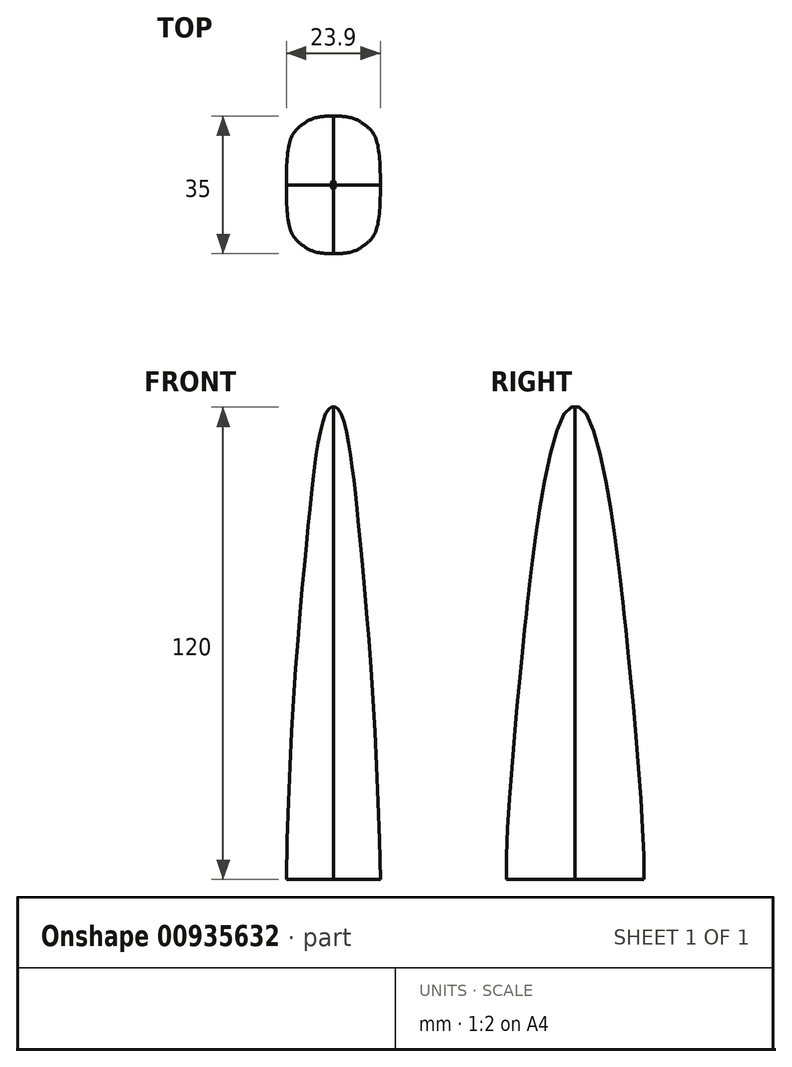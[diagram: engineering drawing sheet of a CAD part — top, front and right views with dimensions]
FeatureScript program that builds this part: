
annotation { "Feature Type Name" : "Feature", "Feature Type Description" : "" }
export const myFeature = defineFeature(function(context is Context, id is Id, definition is map)
    precondition{}
    {
        {
            var Q0;
            Q0=qCreatedBy(makeId("Top.planeOp"),FACE);
            var sketch = newSketch(context, id + "F0", { "sketchPlane" : qUnion([Q0])});
            skLineSegment(sketch, "E0", {"start": v(11.95, 0) * mm, "end": v(11.95, 33.1) * mm, "construction": true});
            skLineSegment(sketch, "E1", {"start": v(11.95, 0) * mm, "end": v(11.95, -38.84) * mm, "construction": true});
            skLineSegment(sketch, "E2", {"start": v(0, 0) * mm, "end": v(11.95, 0) * mm});
            skLineSegment(sketch, "E3", {"start": v(0, 0) * mm, "end": v(0, 17.5) * mm});
            skFitSpline(sketch, "E4", {"points": [v(0, 17.5) * mm, v(6.97, 15.94) * mm, v(9.26, 14.16) * mm, v(11.08, 10.92) * mm, v(11.95, 0) * mm], "startDerivative": vector(48.18, -0.54) * mm, "endDerivative": vector(0, -35.8) * mm});
            skSolve(sketch);
        }
        {
            var Q0;
            Q0=qCreatedBy(makeId("Top.planeOp"),FACE);
            cPlane(context, id + "F1", {"entities" : qUnion([Q0]), "cplaneType" : CPlaneType.OFFSET, "offset" : 120 * mm, "width" : 150 * mm, "height" : 150 * mm});
        }
        {
            var Q0;
            Q0=qCreatedBy(id+"F1.planeOp",FACE);
            var sketch = newSketch(context, id + "F2", { "sketchPlane" : qUnion([Q0])});
            skLineSegment(sketch, "E5", {"start": v(0.5, 0) * mm, "end": v(0.5, 1.93) * mm, "construction": true});
            skLineSegment(sketch, "E6", {"start": v(0.5, 0) * mm, "end": v(0.5, -35.8) * mm, "construction": true});
            skLineSegment(sketch, "E7", {"start": v(0, 0) * mm, "end": v(0.5, 0) * mm});
            skLineSegment(sketch, "E8", {"start": v(0, 0) * mm, "end": v(0, 1) * mm});
            skFitSpline(sketch, "E9", {"points": [v(0, 1) * mm, v(0.19, 0.97) * mm, v(0.3, 0.9) * mm, v(0.4, 0.74) * mm, v(0.5, 0) * mm], "startDerivative": vector(1.93, -0.16) * mm, "endDerivative": vector(0.28, -3.4) * mm});
            skPoint(sketch, "E10", {"position": v(0.5, 0.97) * mm});
            skSolve(sketch);
        }
        {
            var Q0;
            Q0=qCreatedBy(id+"F1.planeOp",FACE);
            cPlane(context, id + "F3", {"entities" : qUnion([Q0]), "cplaneType" : CPlaneType.OFFSET, "offset" : 10 * mm, "width" : 150 * mm, "height" : 150 * mm});
        }
        {
            var Q0;
            Q0=sQuery(id+"F2.wireOp",VERTEX,"E7.start");
            var Q1;
            Q1=sQuery(id+"F2.wireOp",VERTEX,"E9.1.internal");
            var Q2;
            Q2=sQuery(id+"F0.wireOp",VERTEX,"E4.2.internal");
            cPlane(context, id + "F4", {"entities" : qUnion([Q0, Q1, Q2]), "cplaneType" : CPlaneType.THREE_POINT, "offset" : 25 * mm, "width" : 150 * mm, "height" : 150 * mm});
        }
        {
            var Q0;
            Q0=qCreatedBy(makeId("Right.planeOp"),FACE);
            var sketch = newSketch(context, id + "F5", { "sketchPlane" : qUnion([Q0])});
            skFitSpline(sketch, "E11", {"points": [v(17.5, 0) * mm, v(12.57, 65.87) * mm, v(11.75, 73.45) * mm, v(11.28, 77.75) * mm, v(1, 120) * mm], "startDerivative": vector(1.02, 126.16) * mm, "endDerivative": vector(-44.43, 4.7) * mm});
            skSolve(sketch);
        }
        {
            var Q0;
            Q0=qCreatedBy(id+"F4.planeOp",FACE);
            var sketch = newSketch(context, id + "F6", { "sketchPlane" : qUnion([Q0])});
            skFitSpline(sketch, "E12", {"points": [v(2.23, 119.81) * mm, v(4.54, 116.84) * mm, v(6.47, 110.54) * mm, v(8.91, 96.38) * mm, v(12.6, 57.56) * mm, v(15.67, -0.5) * mm], "startDerivative": vector(24.73, -1.78) * mm, "endDerivative": vector(0.35, -291.75) * mm});
            skSolve(sketch);
        }
        {
            var Q0;
            Q0=qCreatedBy(makeId("Front.planeOp"),FACE);
            var sketch = newSketch(context, id + "F7", { "sketchPlane" : qUnion([Q0])});
            skFitSpline(sketch, "E13", {"points": [v(11.95, 0) * mm, v(6.43, 89.6) * mm, v(4.08, 109.75) * mm, v(1.52, 119.15) * mm, v(0.5, 120) * mm], "startDerivative": vector(-4.37, 236.52) * mm, "endDerivative": vector(-10.1, 0.23) * mm});
            skSolve(sketch);
        }
        {
            var Q0;
            Q0=makeQuery(id+"F0.imprint","IMPRINT",FACE,{"disambiguationData":[TD([[makeQuery(id+"F0.imprint","IMPRINT",EDGE,{"derivedFrom":sQuery(id+"F0.wireOp",EDGE,"E2")}),1.0]])]});
            var Q1;
            Q1=makeQuery(id+"F2.imprint","IMPRINT",FACE,{"disambiguationData":[TD([[makeQuery(id+"F2.imprint","IMPRINT",EDGE,{"derivedFrom":sQuery(id+"F2.wireOp",EDGE,"E7")}),1.0]])]});
            var Q2;
            Q2=sQuery(id+"F6.wireOp",EDGE,"E12");
            var Q3;
            Q3=sQuery(id+"F5.wireOp",EDGE,"E11");
            var Q4;
            Q4=sQuery(id+"F7.wireOp",EDGE,"E13");
            var Q5;
            Q5=sQuery(id+"F6.wireOp",EDGE,"E12");
            loft(context, id + "F8", {"sheetProfilesArray" : [{ "sheetProfileEntities" : qUnion([Q0]) }, { "sheetProfileEntities" : qUnion([Q1]) }], "addGuides" : true, "guidesArray" : [{ "guideEntities" : qUnion([Q2]), "guideDerivativeType" : LoftGuideDerivativeType.DEFAULT, "guideDerivativeMagnitude" : 1 }, { "guideEntities" : qUnion([Q3]), "guideDerivativeType" : LoftGuideDerivativeType.DEFAULT, "guideDerivativeMagnitude" : 1 }, { "guideEntities" : qUnion([Q4]), "guideDerivativeType" : LoftGuideDerivativeType.DEFAULT, "guideDerivativeMagnitude" : 1 }], "spine" : qUnion([Q5])});
        }
        {
            var Q0;
            Q0=makeQuery(id+"F8.opLoft","SWEPT_BODY",BODY,{"disambiguationData":[OSD([makeQuery(id+"F0.imprint","IMPRINT",FACE,{"disambiguationData":[TD([[makeQuery(id+"F0.imprint","IMPRINT",EDGE,{"derivedFrom":sQuery(id+"F0.wireOp",EDGE,"E2")}),1.0]])]}),makeQuery(id+"F2.imprint","IMPRINT",FACE,{"disambiguationData":[TD([[makeQuery(id+"F2.imprint","IMPRINT",EDGE,{"derivedFrom":sQuery(id+"F2.wireOp",EDGE,"E7")}),1.0]])]}),sQuery(id+"F6.wireOp",EDGE,"E12")])]});
            var Q1;
            Q1=qCreatedBy(makeId("Right.planeOp"),FACE);
            mirror(context, id + "F9", {"operationType" : NewBodyOperationType.ADD, "entities" : qUnion([Q0]), "mirrorPlane" : qUnion([Q1])});
        }
        {
            var Q0;
            Q0=makeQuery(id+"F8.opLoft","SWEPT_BODY",BODY,{"disambiguationData":[OSD([makeQuery(id+"F0.imprint","IMPRINT",FACE,{"disambiguationData":[TD([[makeQuery(id+"F0.imprint","IMPRINT",EDGE,{"derivedFrom":sQuery(id+"F0.wireOp",EDGE,"E2")}),1.0]])]}),makeQuery(id+"F2.imprint","IMPRINT",FACE,{"disambiguationData":[TD([[makeQuery(id+"F2.imprint","IMPRINT",EDGE,{"derivedFrom":sQuery(id+"F2.wireOp",EDGE,"E7")}),1.0]])]}),sQuery(id+"F6.wireOp",EDGE,"E12")])]});
            var Q1;
            Q1=qCreatedBy(makeId("Front.planeOp"),FACE);
            mirror(context, id + "F10", {"operationType" : NewBodyOperationType.ADD, "entities" : qUnion([Q0]), "mirrorPlane" : qUnion([Q1])});
        }
    });
